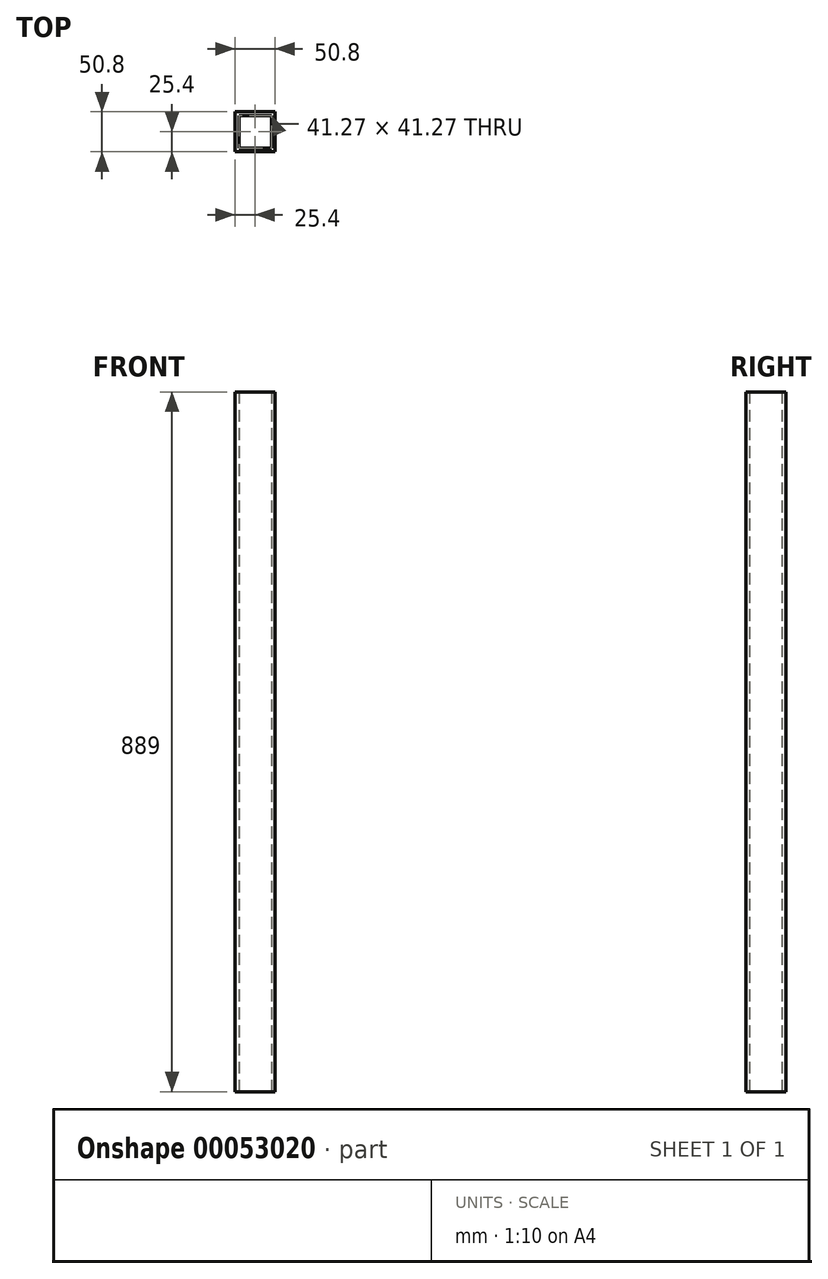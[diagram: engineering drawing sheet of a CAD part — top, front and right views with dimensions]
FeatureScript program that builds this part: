
annotation { "Feature Type Name" : "Feature", "Feature Type Description" : "" }
export const myFeature = defineFeature(function(context is Context, id is Id, definition is map)
    precondition{}
    {
        {
            var Q0;
            Q0=qCreatedBy(makeId("Top.planeOp"),FACE);
            var sketch = newSketch(context, id + "F0", { "sketchPlane" : qUnion([Q0])});
            skLineSegment(sketch, "E0.bottom", {"start": v(0, 0) * mm, "end": v(-50.8, 0) * mm});
            skLineSegment(sketch, "E0.top", {"start": v(0, 50.8) * mm, "end": v(-50.8, 50.8) * mm});
            skLineSegment(sketch, "E0.left", {"start": v(0, 0) * mm, "end": v(0, 50.8) * mm});
            skLineSegment(sketch, "E0.right", {"start": v(-50.8, 0) * mm, "end": v(-50.8, 50.8) * mm});
            skLineSegment(sketch, "E1.bottom", {"start": v(-4.76, 4.76) * mm, "end": v(-46.04, 4.76) * mm});
            skLineSegment(sketch, "E1.top", {"start": v(-4.76, 46.04) * mm, "end": v(-46.04, 46.04) * mm});
            skLineSegment(sketch, "E1.left", {"start": v(-4.76, 4.76) * mm, "end": v(-4.76, 46.04) * mm});
            skLineSegment(sketch, "E1.right", {"start": v(-46.04, 4.76) * mm, "end": v(-46.04, 46.04) * mm});
            skSolve(sketch);
        }
        {
            var Q0;
            Q0=makeQuery(id+"F0.imprint","IMPRINT",FACE,{"disambiguationData":[TD([[makeQuery(id+"F0.imprint","IMPRINT",EDGE,{"derivedFrom":sQuery(id+"F0.wireOp",EDGE,"E0.bottom")}),-1.0]])]});
            extrude(context, id + "F1", {"entities" : qUnion([Q0]), "depth" : 889 * mm});
        }
    });
